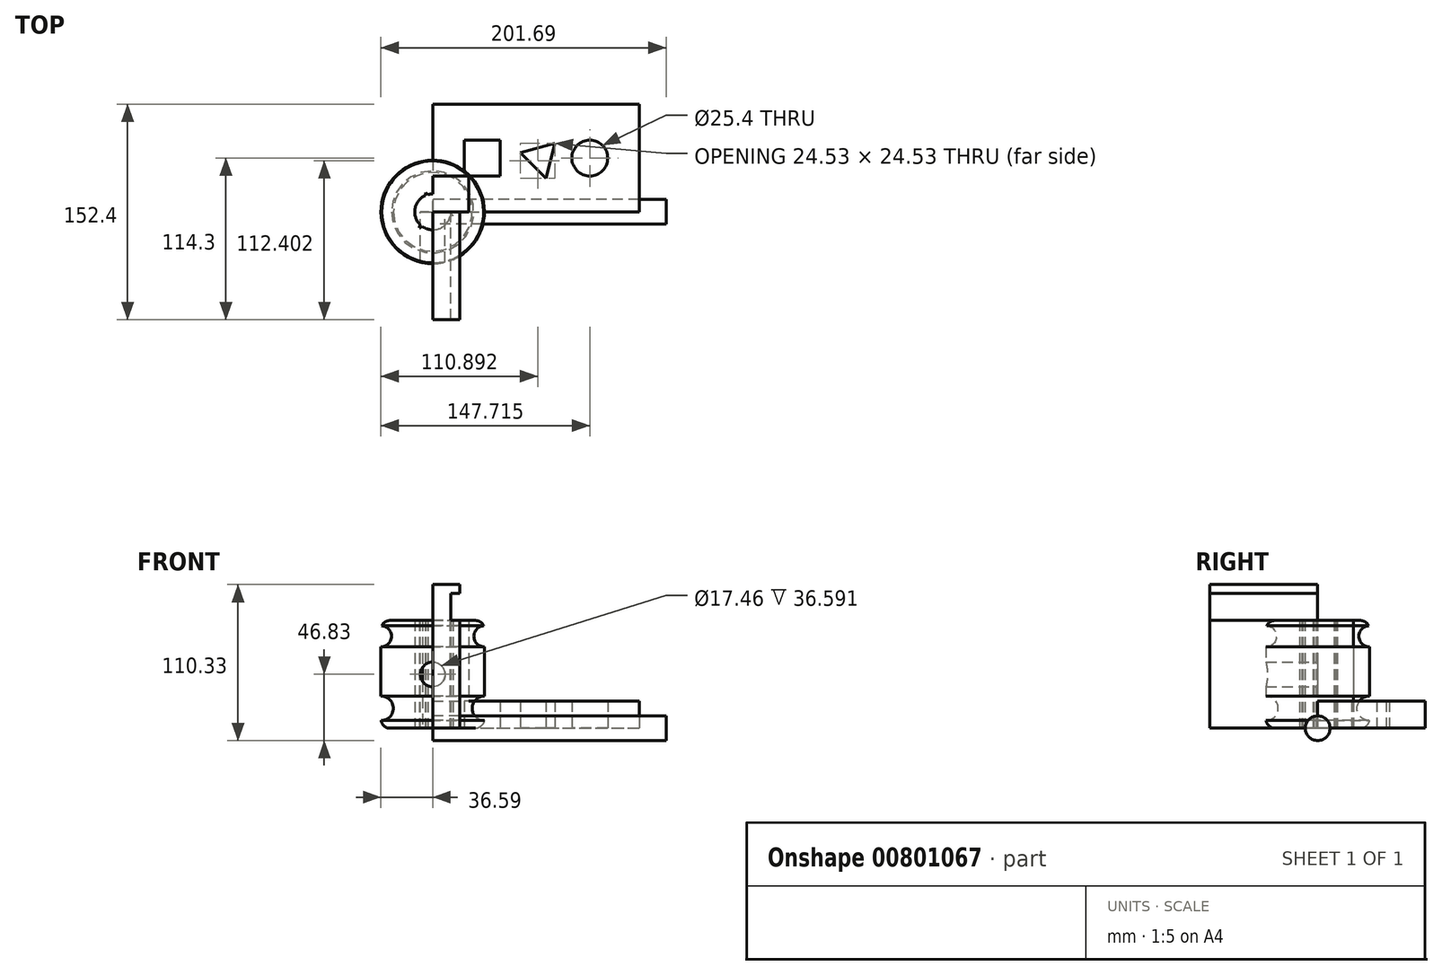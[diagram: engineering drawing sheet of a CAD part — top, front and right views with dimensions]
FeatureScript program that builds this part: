
annotation { "Feature Type Name" : "Feature", "Feature Type Description" : "" }
export const myFeature = defineFeature(function(context is Context, id is Id, definition is map)
    precondition{}
    {
        {
            var Q0;
            Q0=qCreatedBy(makeId("Top.planeOp"),FACE);
            var sketch = newSketch(context, id + "F0", { "sketchPlane" : qUnion([Q0])});
            skCircle(sketch, "E0", {"center": v(0, 0) * mm, "radius": 12.7 * mm});
            skLineSegment(sketch, "E1.bottom", {"start": v(-12.7, -12.7) * mm, "end": v(12.7, -12.7) * mm});
            skLineSegment(sketch, "E1.top", {"start": v(-12.7, 12.7) * mm, "end": v(12.7, 12.7) * mm});
            skLineSegment(sketch, "E1.left", {"start": v(-12.7, -12.7) * mm, "end": v(-12.7, 12.7) * mm});
            skLineSegment(sketch, "E1.right", {"start": v(12.7, -12.7) * mm, "end": v(12.7, 12.7) * mm});
            skSolve(sketch);
        }
        {
            var Q0;
            Q0=makeQuery(id+"F0.imprint","IMPRINT",FACE,{"disambiguationData":[TD([[makeQuery(id+"F0.imprint","IMPRINT",EDGE,{"derivedFrom":sQuery(id+"F0.wireOp",EDGE,"E0")}),1.0]])]});
            extrude(context, id + "F1", {"entities" : qUnion([Q0]), "depth" : 76.2 * mm, "offsetDistance" : 25.4 * mm});
        }
        {
            var Q0;
            Q0=qCreatedBy(makeId("Top.planeOp"),FACE);
            var sketch = newSketch(context, id + "F2", { "sketchPlane" : qUnion([Q0])});
            skLineSegment(sketch, "E2.bottom", {"start": v(0, 0) * mm, "end": v(25.4, 0) * mm});
            skLineSegment(sketch, "E2.top", {"start": v(0, 25.4) * mm, "end": v(25.4, 25.4) * mm});
            skLineSegment(sketch, "E2.left", {"start": v(0, 0) * mm, "end": v(0, 25.4) * mm});
            skLineSegment(sketch, "E2.right", {"start": v(25.4, 0) * mm, "end": v(25.4, 25.4) * mm});
            skSolve(sketch);
        }
        {
            var Q0;
            Q0 = qSketchRegion(id + "F2", true);
            extrude(context, id + "F3", {"entities" : qUnion([Q0]), "depth" : 25.4 * mm, "offsetDistance" : 25.4 * mm});
        }
        {
            var Q0;
            Q0 = qSketchRegion(id + "F2", true);
            extrude(context, id + "F4", {"entities" : qUnion([Q0]), "operationType" : NewBodyOperationType.ADD, "depth" : 76.2 * mm, "offsetDistance" : 25.4 * mm});
        }
        {
            var Q0;
            Q0=qCreatedBy(makeId("Top.planeOp"),FACE);
            var sketch = newSketch(context, id + "F5", { "sketchPlane" : qUnion([Q0])});
            skCircle(sketch, "E3.cCircle", {"center": v(0, 0) * mm, "radius": 7.33 * mm, "construction": true});
            skLineSegment(sketch, "E3.0", {"start": v(-5.05, 13.77) * mm, "end": v(14.45, -2.51) * mm});
            skLineSegment(sketch, "E3.1", {"start": v(14.45, -2.51) * mm, "end": v(-9.4, -11.25) * mm});
            skLineSegment(sketch, "E3.2", {"start": v(-9.4, -11.25) * mm, "end": v(-5.05, 13.77) * mm});
            skPoint(sketch, "E3.0.midPoint", {"position": v(4.7, 5.63) * mm});
            skSolve(sketch);
        }
        {
            var Q0;
            Q0 = qSketchRegion(id + "F5", true);
            extrude(context, id + "F6", {"entities" : qUnion([Q0]), "depth" : 76.2 * mm, "offsetDistance" : 25.4 * mm});
        }
        {
            var Q0;
            Q0=qCreatedBy(makeId("Top.planeOp"),FACE);
            var sketch = newSketch(context, id + "F7", { "sketchPlane" : qUnion([Q0])});
            skLineSegment(sketch, "E4.bottom", {"start": v(0, 76.2) * mm, "end": v(146.05, 76.2) * mm});
            skLineSegment(sketch, "E4.top", {"start": v(0, 0) * mm, "end": v(146.05, 0) * mm});
            skLineSegment(sketch, "E4.left", {"start": v(0, 76.2) * mm, "end": v(0, 0) * mm});
            skLineSegment(sketch, "E4.right", {"start": v(146.05, 76.2) * mm, "end": v(146.05, 0) * mm});
            skCircle(sketch, "E5", {"center": v(111.12, 38.1) * mm, "radius": 12.7 * mm});
            skCircle(sketch, "E6.cCircle", {"center": v(76.2, 38.1) * mm, "radius": 7.33 * mm, "construction": true});
            skLineSegment(sketch, "E6.0", {"start": v(86.57, 48.47) * mm, "end": v(80, 23.93) * mm});
            skLineSegment(sketch, "E6.1", {"start": v(80, 23.93) * mm, "end": v(62.03, 41.9) * mm});
            skLineSegment(sketch, "E6.2", {"start": v(62.03, 41.9) * mm, "end": v(86.57, 48.47) * mm});
            skPoint(sketch, "E6.0.midPoint", {"position": v(83.28, 36.2) * mm});
            skLineSegment(sketch, "E7.bottom", {"start": v(47.63, 25.4) * mm, "end": v(22.23, 25.4) * mm});
            skLineSegment(sketch, "E7.top", {"start": v(47.63, 50.8) * mm, "end": v(22.23, 50.8) * mm});
            skLineSegment(sketch, "E7.left", {"start": v(47.63, 25.4) * mm, "end": v(47.63, 50.8) * mm});
            skLineSegment(sketch, "E7.right", {"start": v(22.23, 25.4) * mm, "end": v(22.23, 50.8) * mm});
            skPoint(sketch, "E7.middle", {"position": v(34.93, 38.1) * mm});
            skPoint(sketch, "E7.middle.positionSnap0", {"position": v(0, 38.1) * mm});
            skPoint(sketch, "E7.centerSnap0", {"position": v(0, 38.1) * mm});
            skSolve(sketch);
        }
        {
            var Q0;
            Q0 = qSketchRegion(id + "F7", true);
            extrude(context, id + "F8", {"entities" : qUnion([Q0]), "depth" : 19.05 * mm, "offsetDistance" : 25.4 * mm});
        }
        {
            var Q0;
            Q0 = qSketchRegion(id + "F7", true);
            extrude(context, id + "F9", {"entities" : qUnion([Q0]), "operationType" : NewBodyOperationType.ADD, "depth" : 19.05 * mm, "offsetDistance" : 25.4 * mm});
        }
        {
            var Q0;
            Q0=qCreatedBy(makeId("Front.planeOp"),FACE);
            var sketch = newSketch(context, id + "F10", { "sketchPlane" : qUnion([Q0])});
            skLineSegment(sketch, "E8.bottom", {"start": v(0, 0) * mm, "end": v(19.05, 0) * mm});
            skLineSegment(sketch, "E8.top", {"start": v(0, 101.6) * mm, "end": v(19.05, 101.6) * mm});
            skLineSegment(sketch, "E8.left", {"start": v(0, 0) * mm, "end": v(0, 101.6) * mm});
            skLineSegment(sketch, "E8.right", {"start": v(19.05, 0) * mm, "end": v(19.05, 101.6) * mm});
            skLineSegment(sketch, "E9.bottom", {"start": v(19.05, 95.25) * mm, "end": v(12.7, 95.25) * mm});
            skLineSegment(sketch, "E9.top", {"start": v(19.05, 76.2) * mm, "end": v(12.7, 76.2) * mm});
            skLineSegment(sketch, "E9.left", {"start": v(19.05, 95.25) * mm, "end": v(19.05, 76.2) * mm});
            skLineSegment(sketch, "E9.right", {"start": v(12.7, 95.25) * mm, "end": v(12.7, 76.2) * mm});
            skSolve(sketch);
        }
        {
            var Q0;
            {var subQ1=sQuery(id+"F10.wireOp",EDGE,"E8.bottom");Q0=makeQuery(id+"F10.imprint","IMPRINT",FACE,{"disambiguationData":[TD([[makeQuery(id+"F10.imprint","IMPRINT",EDGE,{"derivedFrom":subQ1}),1.0]])]});}
            extrude(context, id + "F11", {"entities" : qUnion([Q0]), "depth" : 76.2 * mm, "offsetDistance" : 25.4 * mm});
        }
        {
            var Q0;
            Q0=qCreatedBy(makeId("Front.planeOp"),FACE);
            var sketch = newSketch(context, id + "F12", { "sketchPlane" : qUnion([Q0])});
            skLineSegment(sketch, "E10.bottom", {"start": v(0, 0) * mm, "end": v(30.24, 0) * mm});
            skLineSegment(sketch, "E10.top", {"start": v(0, 76.2) * mm, "end": v(30.24, 76.2) * mm});
            skLineSegment(sketch, "E10.left", {"start": v(0, 0) * mm, "end": v(0, 76.2) * mm});
            skLineSegment(sketch, "E10.right", {"start": v(36.59, 6.35) * mm, "end": v(36.59, 69.85) * mm});
            skCircle(sketch, "E11", {"center": v(36.59, 65.05) * mm, "radius": 7.47 * mm});
            skCircle(sketch, "E12", {"center": v(36.59, 14.08) * mm, "radius": 8.69 * mm});
            skPoint(sketch, "E13.visualSharp", {"position": v(36.59, 76.2) * mm});
            skArc(sketch, "E13.filletArc", {"start": v(36.59, 69.85) * mm, "mid": v(34.73, 74.34) * mm, "end": v(30.24, 76.2) * mm});
            skPoint(sketch, "E14.visualSharp", {"position": v(36.59, 0) * mm});
            skArc(sketch, "E14.filletArc", {"start": v(30.24, 0) * mm, "mid": v(34.73, 1.86) * mm, "end": v(36.59, 6.35) * mm});
            skSolve(sketch);
        }
        {
            var Q0;
            {var subQ7=sQuery(id+"F12.wireOp",EDGE,"E10.bottom");Q0=makeQuery(id+"F12.imprint","IMPRINT",FACE,{"disambiguationData":[TD([[makeQuery(id+"F12.imprint","IMPRINT",EDGE,{"derivedFrom":subQ7}),1.0]])]});}
            var Q1;
            Q1=sQuery(id+"F12.wireOp",EDGE,"E10.left");
            revolve(context, id + "F13", {"surfaceOperationType" : NewSurfaceOperationType.NEW, "entities" : qUnion([Q0]), "axis" : qUnion([Q1]), "revolveType" : RevolveType.FULL});
        }
        {
            var Q0;
            Q0=qCreatedBy(makeId("Front.planeOp"),FACE);
            var sketch = newSketch(context, id + "F14", { "sketchPlane" : qUnion([Q0])});
            skPoint(sketch, "E15", {"position": v(0, 38.1) * mm});
            skSolve(sketch);
        }
        {
            var Q0;
            Q0=sQuery(id+"F14.wireOp",VERTEX,"E15");
            var Q1;
            Q1=makeQuery(id+"F13.opRevolve","SWEPT_BODY",BODY,{"disambiguationData":[OSD([sQuery(id+"F12.wireOp",EDGE,"E10.bottom"),sQuery(id+"F12.wireOp",EDGE,"E10.top"),sQuery(id+"F12.wireOp",EDGE,"E10.left"),sQuery(id+"F12.wireOp",EDGE,"E10.right"),sQuery(id+"F12.wireOp",EDGE,"E11"),sQuery(id+"F12.wireOp",EDGE,"E12"),sQuery(id+"F12.wireOp",EDGE,"E13.filletArc"),sQuery(id+"F12.wireOp",EDGE,"E14.filletArc")])]});
            hole(context, id + "F15", {"style" : HoleStyle.SIMPLE, "endStyle" : HoleEndStyle.THROUGH, "oppositeDirection" : true, "standardTappedOrClearance" : lookupTablePath({ "standard" : "ANSI", "engagement" : "75%", "pitch" : "16 tpi", "size" : "3/4", "type" : "Tapped" }), "standardBlindInLast" : lookupTablePath({ "standard" : "ANSI", "engagement" : "75%", "pitch" : "16 tpi", "size" : "3/4", "type" : "Tapped" }), "holeDiameter" : 17.46 * mm, "majorDiameter" : 19.05 * mm, "showTappedDepth" : true, "isTappedThrough" : true, "tappedDepth" : 12.7 * mm, "tapClearance" : 3, "locations" : qUnion([Q0]), "scope" : qUnion([Q1])});
        }
        {
            var Q0;
            Q0=qCreatedBy(makeId("Right.planeOp"),FACE);
            var sketch = newSketch(context, id + "F16", { "sketchPlane" : qUnion([Q0])});
            skCircle(sketch, "E16", {"center": v(0, 0) * mm, "radius": 8.73 * mm});
            skSolve(sketch);
        }
        {
            var Q0;
            Q0=makeQuery(id+"F16.imprint","IMPRINT",FACE,{"disambiguationData":[TD([[makeQuery(id+"F16.imprint","IMPRINT",EDGE,{"derivedFrom":sQuery(id+"F16.wireOp",EDGE,"E16")}),1.0]])]});
            extrude(context, id + "F17", {"entities" : qUnion([Q0]), "depth" : 165.1 * mm, "offsetDistance" : 25.4 * mm});
        }
    });
